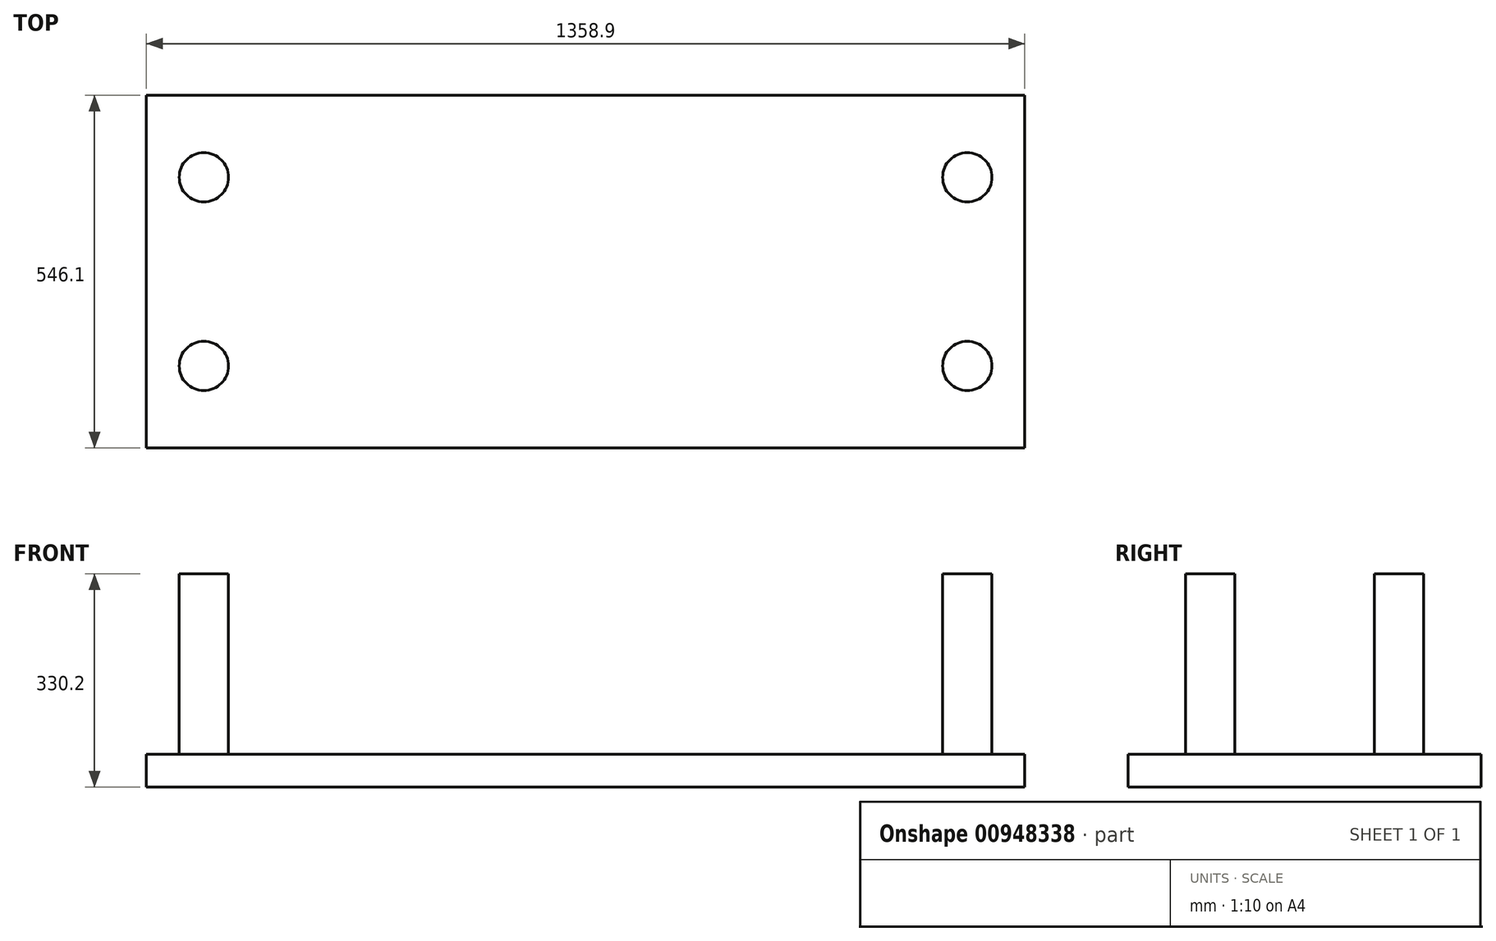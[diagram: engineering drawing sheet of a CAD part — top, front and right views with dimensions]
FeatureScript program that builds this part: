
annotation { "Feature Type Name" : "Feature", "Feature Type Description" : "" }
export const myFeature = defineFeature(function(context is Context, id is Id, definition is map)
    precondition{}
    {
        {
            var Q0;
            Q0=qCreatedBy(makeId("Top.planeOp"),FACE);
            var sketch = newSketch(context, id + "F0", { "sketchPlane" : qUnion([Q0])});
            skLineSegment(sketch, "E0", {"start": v(0, 0) * mm, "end": v(0, 546.1) * mm});
            skLineSegment(sketch, "E1", {"start": v(0, 546.1) * mm, "end": v(1358.9, 546.1) * mm});
            skLineSegment(sketch, "E2", {"start": v(1358.9, 546.1) * mm, "end": v(1358.9, 0) * mm});
            skLineSegment(sketch, "E3", {"start": v(1358.9, 0) * mm, "end": v(0, 0) * mm});
            skSolve(sketch);
        }
        {
            var Q0;
            Q0=makeQuery(id+"F0.imprint","IMPRINT",FACE,{"disambiguationData":[TD([[makeQuery(id+"F0.imprint","IMPRINT",EDGE,{"derivedFrom":sQuery(id+"F0.wireOp",EDGE,"E0")}),-1.0]])]});
            extrude(context, id + "F1", {"entities" : qUnion([Q0]), "depth" : 50.8 * mm, "offsetDistance" : 25.4 * mm});
        }
        {
            var Q0;
            Q0=makeQuery(id+"F1.opExtrude","CAP_FACE",FACE,{"disambiguationData":[OSD([sQuery(id+"F0.wireOp",EDGE,"E0"),sQuery(id+"F0.wireOp",EDGE,"E1"),sQuery(id+"F0.wireOp",EDGE,"E2"),sQuery(id+"F0.wireOp",EDGE,"E3")])],"isStart":true});
            var sketch = newSketch(context, id + "F2", { "sketchPlane" : qUnion([Q0])});
            skCircle(sketch, "E4", {"center": v(88.9, -127) * mm, "radius": 38.1 * mm});
            skCircle(sketch, "E5", {"center": v(1270, -127) * mm, "radius": 38.1 * mm});
            skCircle(sketch, "E6", {"center": v(88.9, -419.1) * mm, "radius": 38.1 * mm});
            skCircle(sketch, "E7", {"center": v(1270, -419.1) * mm, "radius": 38.1 * mm});
            skSolve(sketch);
        }
        {
            var Q0;
            Q0 = qSketchRegion(id + "F2", true);
            extrude(context, id + "F3", {"entities" : qUnion([Q0]), "operationType" : NewBodyOperationType.ADD, "oppositeDirection" : true, "depth" : 330.2 * mm, "offsetDistance" : 25.4 * mm});
        }
    });
